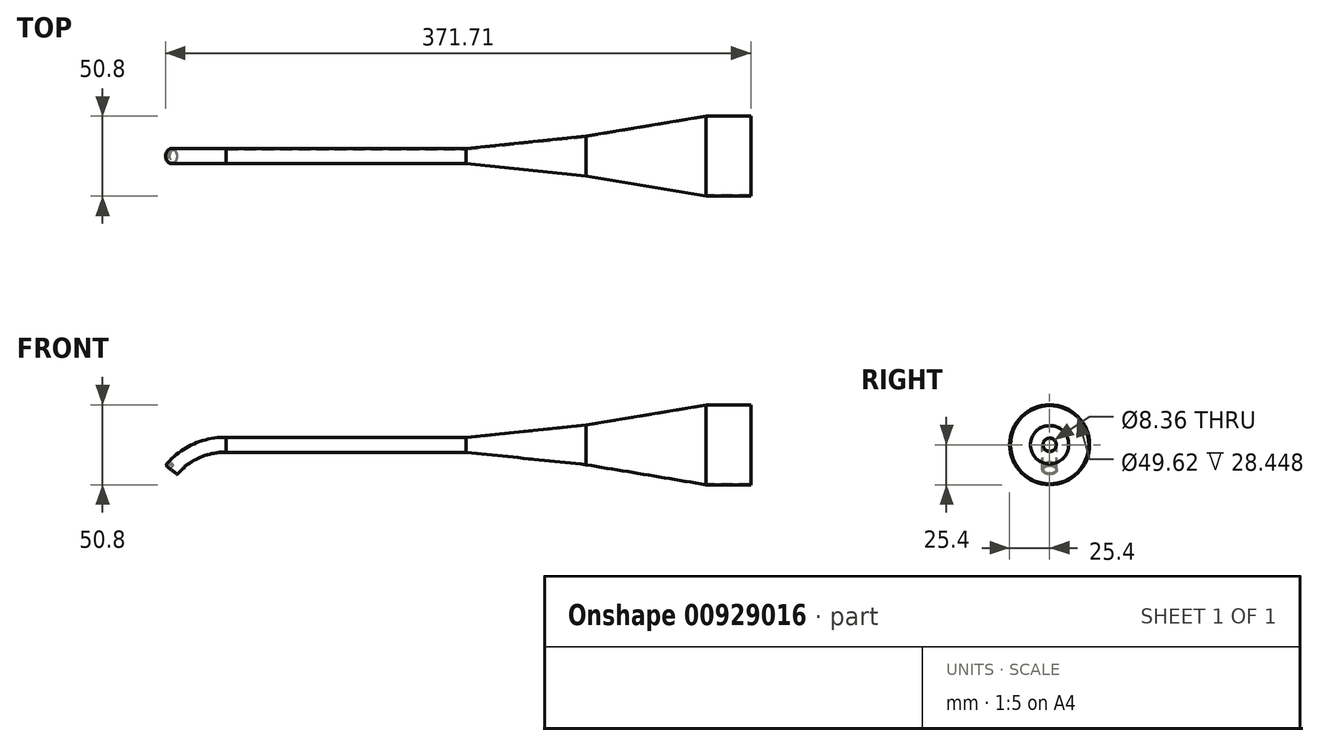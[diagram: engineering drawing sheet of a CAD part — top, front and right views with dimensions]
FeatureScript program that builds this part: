
annotation { "Feature Type Name" : "Feature", "Feature Type Description" : "" }
export const myFeature = defineFeature(function(context is Context, id is Id, definition is map)
    precondition{}
    {
        {
            var Q0;
            Q0=qCreatedBy(makeId("Right.planeOp"),FACE);
            var sketch = newSketch(context, id + "F0", { "sketchPlane" : qUnion([Q0])});
            skCircle(sketch, "E0", {"center": v(0, 0) * mm, "radius": 4.76 * mm});
            skSolve(sketch);
        }
        {
            var Q0;
            Q0=qCreatedBy(makeId("Right.planeOp"),FACE);
            cPlane(context, id + "F1", {"entities" : qUnion([Q0]), "cplaneType" : CPlaneType.OFFSET, "offset" : 76.2 * mm, "width" : 152.4 * mm, "height" : 152.4 * mm});
        }
        {
            var Q0;
            Q0=makeQuery(id+"F0.imprint","IMPRINT",FACE,{"disambiguationData":[TD([[makeQuery(id+"F0.imprint","IMPRINT",EDGE,{"derivedFrom":sQuery(id+"F0.wireOp",EDGE,"E0")}),1.0]])]});
            extrude(context, id + "F2", {"entities" : qUnion([Q0]), "oppositeDirection" : true, "depth" : 152.4 * mm, "offsetDistance" : 25.4 * mm});
        }
        {
            var Q0;
            Q0=qCreatedBy(id+"F1.planeOp",FACE);
            var sketch = newSketch(context, id + "F3", { "sketchPlane" : qUnion([Q0])});
            skCircle(sketch, "E1", {"center": v(0, 0) * mm, "radius": 12.7 * mm});
            skSolve(sketch);
        }
        {
            var Q1;
            Q1=makeQuery(id+"F2.opExtrude","CAP_FACE",FACE,{"disambiguationData":[OSD([sQuery(id+"F0.wireOp",EDGE,"E0")])],"isStart":true});
            var Q2;
            Q2=makeQuery(id+"F3.imprint","IMPRINT",FACE,{"disambiguationData":[TD([[makeQuery(id+"F3.imprint","IMPRINT",EDGE,{"derivedFrom":sQuery(id+"F3.wireOp",EDGE,"E1")}),1.0]])]});
            loft(context, id + "F4", {"operationType" : NewBodyOperationType.ADD, "sheetProfilesArray" : [{ "sheetProfileEntities" : qUnion([Q1]) }, { "sheetProfileEntities" : qUnion([Q2]) }]});
        }
        {
            var Q0;
            Q0=qCreatedBy(id+"F1.planeOp",FACE);
            cPlane(context, id + "F5", {"entities" : qUnion([Q0]), "cplaneType" : CPlaneType.OFFSET, "offset" : 76.2 * mm, "width" : 152.4 * mm, "height" : 152.4 * mm});
        }
        {
            var Q0;
            Q0=qCreatedBy(id+"F5.planeOp",FACE);
            var sketch = newSketch(context, id + "F6", { "sketchPlane" : qUnion([Q0])});
            skCircle(sketch, "E2", {"center": v(0, 0) * mm, "radius": 25.4 * mm});
            skSolve(sketch);
        }
        {
            var Q1;
            Q1=makeQuery(id+"F4.opLoft","CAP_FACE",FACE,{"disambiguationData":[OSD([makeQuery(id+"F3.imprint","IMPRINT",FACE,{"disambiguationData":[TD([[makeQuery(id+"F3.imprint","IMPRINT",EDGE,{"derivedFrom":sQuery(id+"F3.wireOp",EDGE,"E1")}),1.0]])]})])],"isStart":true});
            var Q2;
            Q2=makeQuery(id+"F6.imprint","IMPRINT",FACE,{"disambiguationData":[TD([[makeQuery(id+"F6.imprint","IMPRINT",EDGE,{"derivedFrom":sQuery(id+"F6.wireOp",EDGE,"E2")}),1.0]])]});
            loft(context, id + "F7", {"operationType" : NewBodyOperationType.ADD, "sheetProfilesArray" : [{ "sheetProfileEntities" : qUnion([Q1]) }, { "sheetProfileEntities" : qUnion([Q2]) }]});
        }
        {
            var Q0;
            Q0=qCreatedBy(makeId("Top.planeOp"),FACE);
            cPlane(context, id + "F8", {"entities" : qUnion([Q0]), "cplaneType" : CPlaneType.OFFSET, "offset" : 16 * mm, "oppositeDirection" : true, "width" : 152.4 * mm, "height" : 152.4 * mm});
        }
        {
            var Q0;
            Q0=qCreatedBy(id+"F8.planeOp",FACE);
            var sketch = newSketch(context, id + "F9", { "sketchPlane" : qUnion([Q0])});
            skCircle(sketch, "E3", {"center": v(-187.16, 0) * mm, "radius": 4.76 * mm});
            skSolve(sketch);
        }
        {
            var Q0;
            Q0=qCreatedBy(makeId("Front.planeOp"),FACE);
            var sketch = newSketch(context, id + "F10", { "sketchPlane" : qUnion([Q0])});
            skArc(sketch, "E4", {"start": v(-152.4, 0) * mm, "mid": v(-171.6, -4.07) * mm, "end": v(-187.16, -16) * mm});
            skSolve(sketch);
        }
        {
            var Q0;
            Q0=makeQuery(id+"F2.opExtrude","CAP_FACE",FACE,{"disambiguationData":[OSD([sQuery(id+"F0.wireOp",EDGE,"E0")])],"isStart":false});
            var Q1;
            Q1=sQuery(id+"F10.wireOp",EDGE,"E4");
            var Q2;
            Q2=sQuery(id+"F10.wireOp",EDGE,"E4");
            sweep(context, id + "F11", {"operationType" : NewBodyOperationType.ADD, "profiles" : qUnion([Q0]), "path" : qUnion([Q1, Q2])});
        }
        {
            var Q0;
            Q0=makeQuery(id+"F7.opLoft","CAP_FACE",FACE,{"disambiguationData":[OSD([makeQuery(id+"F6.imprint","IMPRINT",FACE,{"disambiguationData":[TD([[makeQuery(id+"F6.imprint","IMPRINT",EDGE,{"derivedFrom":sQuery(id+"F6.wireOp",EDGE,"E2")}),1.0]])]})])],"isStart":true});
            shell(context, id + "F12", {"entities" : qUnion([Q0]), "thickness" : 0.58 * mm});
        }
        {
            var Q0;
            Q0=makeQuery(id+"F11.opSweep","CAP_FACE",FACE,{"disambiguationData":[OSD([sQuery(id+"F0.wireOp",EDGE,"E0"),sQuery(id+"F10.wireOp",VERTEX,"E4.end")])],"isStart":false});
            var sketch = newSketch(context, id + "F13", { "sketchPlane" : qUnion([Q0])});
            skCircle(sketch, "E5", {"center": v(-135.46, 0) * mm, "radius": 4.14 * mm});
            skSolve(sketch);
        }
        {
            var Q0;
            Q0 = qSketchRegion(id + "F13", true);
            extrude(context, id + "F14", {"entities" : qUnion([Q0]), "operationType" : NewBodyOperationType.REMOVE, "oppositeDirection" : true, "depth" : 3.28 * mm, "offsetDistance" : 25.4 * mm});
        }
        {
            var Q0;
            Q0=makeQuery(id+"F14.boolean.opBoolean","COPY",FACE,{"derivedFrom":makeQuery(id+"F14.opExtrude","CAP_FACE",FACE,{"disambiguationData":[OSD([sQuery(id+"F13.wireOp",EDGE,"E5")])],"isStart":false})});
            extrude(context, id + "F15", {"entities" : qUnion([Q0]), "operationType" : NewBodyOperationType.ADD, "depth" : 3.25 * mm, "offsetDistance" : 25.4 * mm});
        }
        {
            var Q0;
            Q0=makeQuery(id+"F7.opLoft","CAP_FACE",FACE,{"disambiguationData":[OSD([makeQuery(id+"F6.imprint","IMPRINT",FACE,{"disambiguationData":[TD([[makeQuery(id+"F6.imprint","IMPRINT",EDGE,{"derivedFrom":sQuery(id+"F6.wireOp",EDGE,"E2")}),1.0]])]})])],"isStart":true});
            extrude(context, id + "F16", {"entities" : qUnion([Q0]), "operationType" : NewBodyOperationType.ADD, "depth" : 28.45 * mm, "offsetDistance" : 25.4 * mm});
        }
    });
